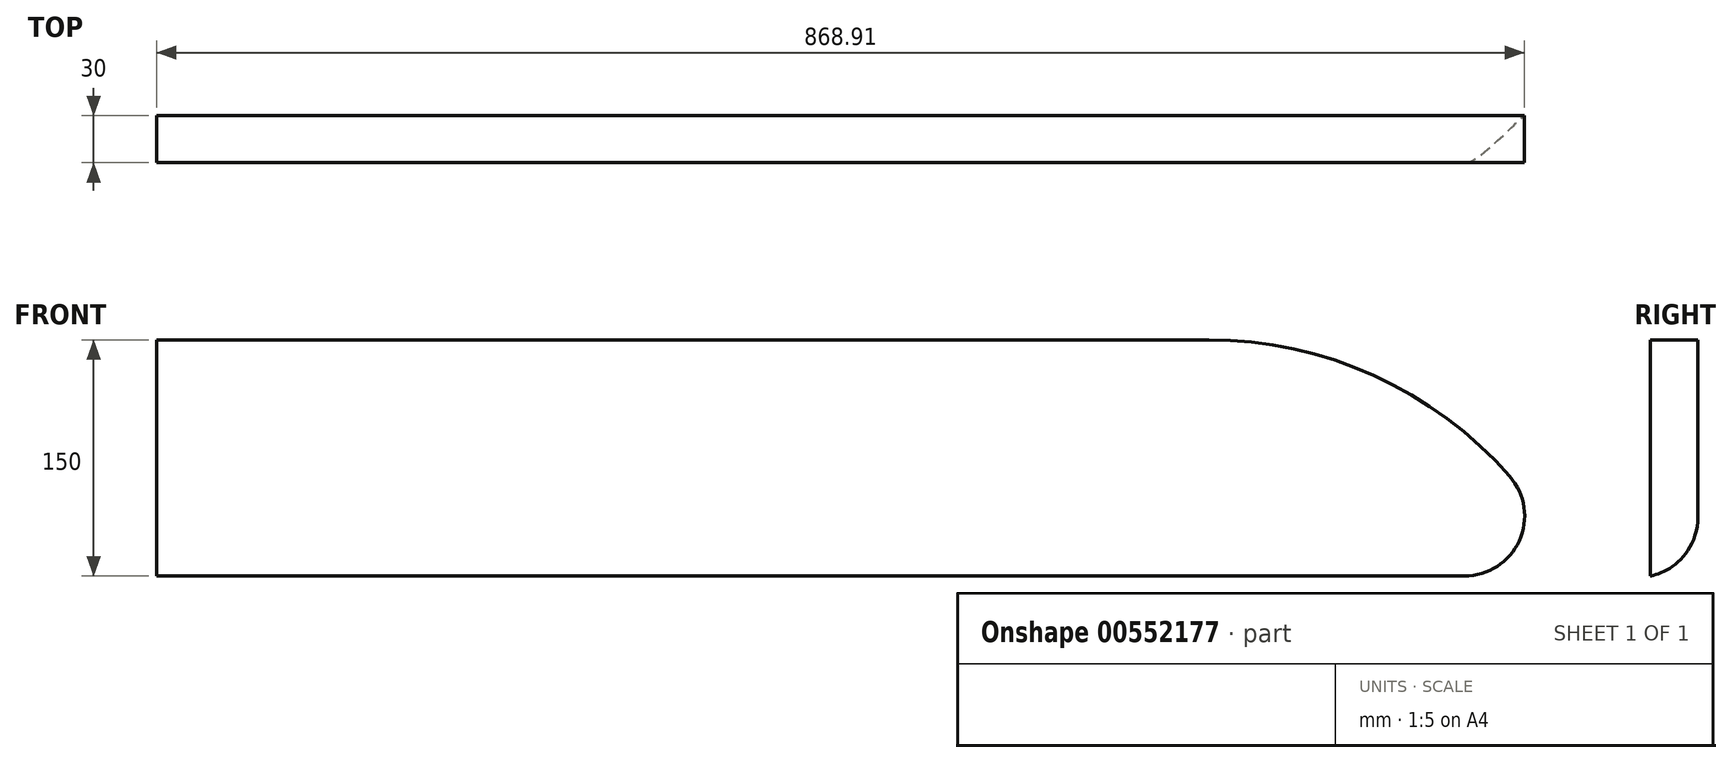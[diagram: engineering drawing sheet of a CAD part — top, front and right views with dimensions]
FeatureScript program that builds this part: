
annotation { "Feature Type Name" : "Feature", "Feature Type Description" : "" }
export const myFeature = defineFeature(function(context is Context, id is Id, definition is map)
    precondition{}
    {
        {
            var Q0;
            Q0=qCreatedBy(makeId("Front.planeOp"),FACE);
            var sketch = newSketch(context, id + "F0", { "sketchPlane" : qUnion([Q0])});
            skLineSegment(sketch, "E0.bottom", {"start": v(0, 0) * mm, "end": v(-900, 0) * mm});
            skLineSegment(sketch, "E0.top", {"start": v(0, -150) * mm, "end": v(-900, -150) * mm});
            skLineSegment(sketch, "E0.left", {"start": v(0, 0) * mm, "end": v(0, -150) * mm});
            skLineSegment(sketch, "E0.right", {"start": v(-900, 0) * mm, "end": v(-900, -150) * mm});
            skSolve(sketch);
        }
        {
            var Q0;
            Q0=makeQuery(id+"F0.imprint","IMPRINT",FACE,{"disambiguationData":[TD([[makeQuery(id+"F0.imprint","IMPRINT",EDGE,{"derivedFrom":sQuery(id+"F0.wireOp",EDGE,"E0.bottom")}),1.0]])]});
            extrude(context, id + "F1", {"entities" : qUnion([Q0]), "depth" : 30 * mm, "offsetDistance" : 25.4 * mm});
        }
        {
            var Q0;
            Q0=makeQuery(id+"F1.opExtrude","SWEPT_EDGE",EDGE,{"disambiguationData":[OSD([sQuery(id+"F0.wireOp",EDGE,"E0.bottom"),sQuery(id+"F0.wireOp",EDGE,"E0.left")])]});
            fillet(context, id + "F2", {"entities" : qUnion([Q0]), "radius" : 254 * mm, "tangentPropagation" : true, "allowEdgeOverflow" : false});
        }
        {
            var Q0;
            Q0=makeQuery(id+"F2.opFillet","BLEND_EDGE",EDGE,{"blendedFrom":[makeQuery(id+"F1.opExtrude","SWEPT_EDGE",EDGE,{"disambiguationData":[OSD([sQuery(id+"F0.wireOp",EDGE,"E0.bottom"),sQuery(id+"F0.wireOp",EDGE,"E0.left")])]}),makeQuery(id+"F1.opExtrude","SWEPT_FACE",FACE,{"disambiguationData":[OSD([sQuery(id+"F0.wireOp",EDGE,"E0.top")])]})],"blendedInto":[makeQuery(id+"F1.opExtrude","SWEPT_FACE",FACE,{"disambiguationData":[OSD([sQuery(id+"F0.wireOp",EDGE,"E0.top")])]})]});
            var Q1;
            Q1=makeQuery(id+"F1.opExtrude","CAP_EDGE",EDGE,{"disambiguationData":[OSD([sQuery(id+"F0.wireOp",EDGE,"E0.top")])],"isStart":true});
            fillet(context, id + "F3", {"entities" : qUnion([Q0, Q1]), "radius" : 38.1 * mm, "tangentPropagation" : true, "allowEdgeOverflow" : false});
        }
    });
